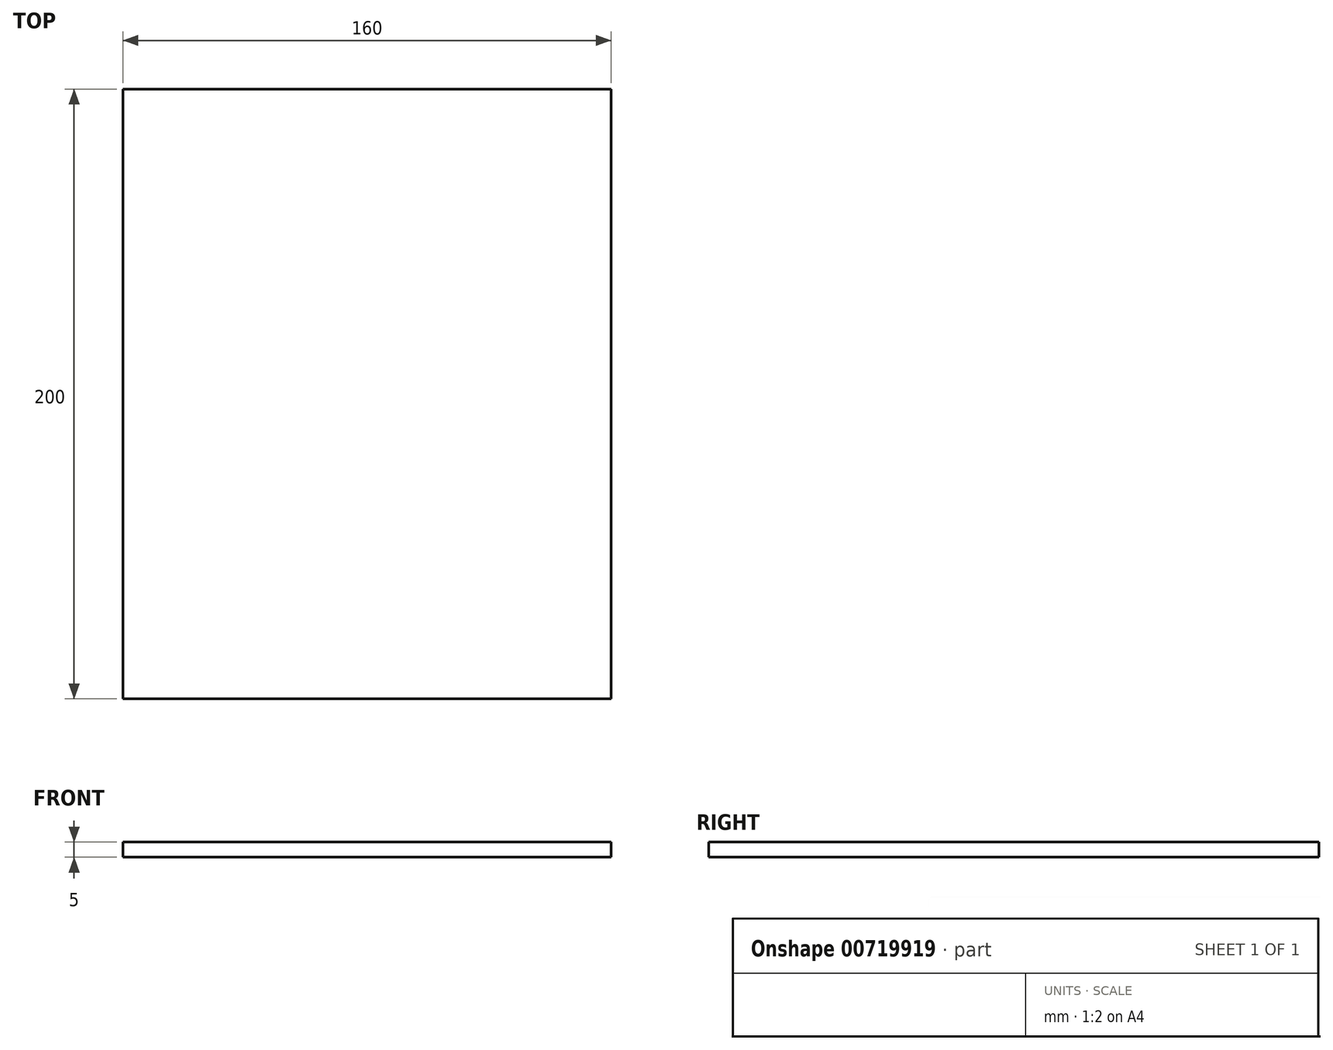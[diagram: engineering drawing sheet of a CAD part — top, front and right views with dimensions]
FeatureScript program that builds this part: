
annotation { "Feature Type Name" : "Feature", "Feature Type Description" : "" }
export const myFeature = defineFeature(function(context is Context, id is Id, definition is map)
    precondition{}
    {
        {
            var Q0;
            Q0=qCreatedBy(makeId("Top.planeOp"),FACE);
            var sketch = newSketch(context, id + "F0", { "sketchPlane" : qUnion([Q0])});
            skLineSegment(sketch, "E0.bottom", {"start": v(0, 0) * mm, "end": v(160, 0) * mm});
            skLineSegment(sketch, "E0.top", {"start": v(0, -200) * mm, "end": v(160, -200) * mm});
            skLineSegment(sketch, "E0.left", {"start": v(0, 0) * mm, "end": v(0, -200) * mm});
            skLineSegment(sketch, "E0.right", {"start": v(160, 0) * mm, "end": v(160, -200) * mm});
            skSolve(sketch);
        }
        {
            var Q0;
            Q0=makeQuery(id+"F0.imprint","IMPRINT",FACE,{"disambiguationData":[TD([[makeQuery(id+"F0.imprint","IMPRINT",EDGE,{"derivedFrom":sQuery(id+"F0.wireOp",EDGE,"E0.bottom")}),-1.0]])]});
            extrude(context, id + "F1", {"entities" : qUnion([Q0]), "depth" : 5 * mm, "offsetDistance" : 25 * mm});
        }
    });
